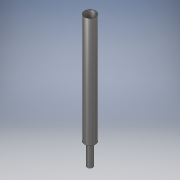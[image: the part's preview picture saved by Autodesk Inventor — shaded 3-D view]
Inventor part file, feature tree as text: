
AUTODESK INVENTOR PART (.ipt)
format: ipt  version: 2018 (Build 220112000, 112)  size: 112,640 bytes
history: native  units: in
note: dims shown in document units (in); Inventor stores cm internally (conversion verified against a paired STEP export)
features: extrude x3, sketch x3
ambient origin geometry x8: Origin, YZ Plane, XZ Plane, XY Plane, X Axis, Y Axis, Z Axis, Center Point
bodies: Solid1 (feature_tree)
feature tree (6):
  extrude  "Extrusion1"  Depth=0.95in
  extrude  "Extrusion2"  Depth=0.5in
  extrude  "Extrusion3"  Depth=0.5in
  sketch  "Sketch1"  dims[d0=1.0in d1=0.95in]
  sketch  "Sketch2"  dims[d2=10.0in d3=0.0in d4=0.5in]
  sketch  "Sketch3"  dims[d5=0.05in d6=0.0in d7=0.5in d8=0.44in d9=2.0in d10=0.0in]
